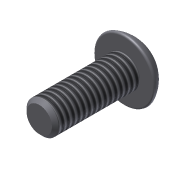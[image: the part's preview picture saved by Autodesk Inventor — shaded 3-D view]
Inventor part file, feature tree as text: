
AUTODESK INVENTOR PART (.ipt)
format: ipt  version: 2011 SP1 (Build 150282100, 282)  size: 126,976 bytes
history: native  units: in
note: dims shown in document units (in); Inventor stores cm internally (conversion verified against a paired STEP export)
features: sketch x3, extrude x2, revolve x1, chamfer x1, thread x1
ambient origin geometry x8: Origin, YZ Plane, XZ Plane, XY Plane, X Axis, Y Axis, Z Axis, Center Point
bodies: Solid1 (feature_tree)
feature tree (8):
  extrude  "Extrusion1"  Depth=0.5in TaperAngle=0.0deg
  revolve  "Revolution1"  [1 undecoded]
  extrude  "Extrusion2"  Depth=0.125in
  chamfer  "Chamfer1"  Distance=0.0625in
  thread  "Thread1"  [1 undecoded]
  sketch  "Sketch1"  dims[d0=0.19in d1=0.5in d2=0.0in]
  sketch  "Sketch2"  dims[d3=0.101in d6=0.08in]
  sketch  "Sketch3"  dims[d7=90.0deg d8=0.125in d9=0.0625in d10=0.0in d12=0.1805in d13=0.02in d14=0.125in d15=45.0deg d16=1.0in d17=0.0in]
note: 2 required parameter values undecoded (feature->parameter linkage not recoverable at this tier; creation-order binding heuristic only, values carry confidence <= 0.55)